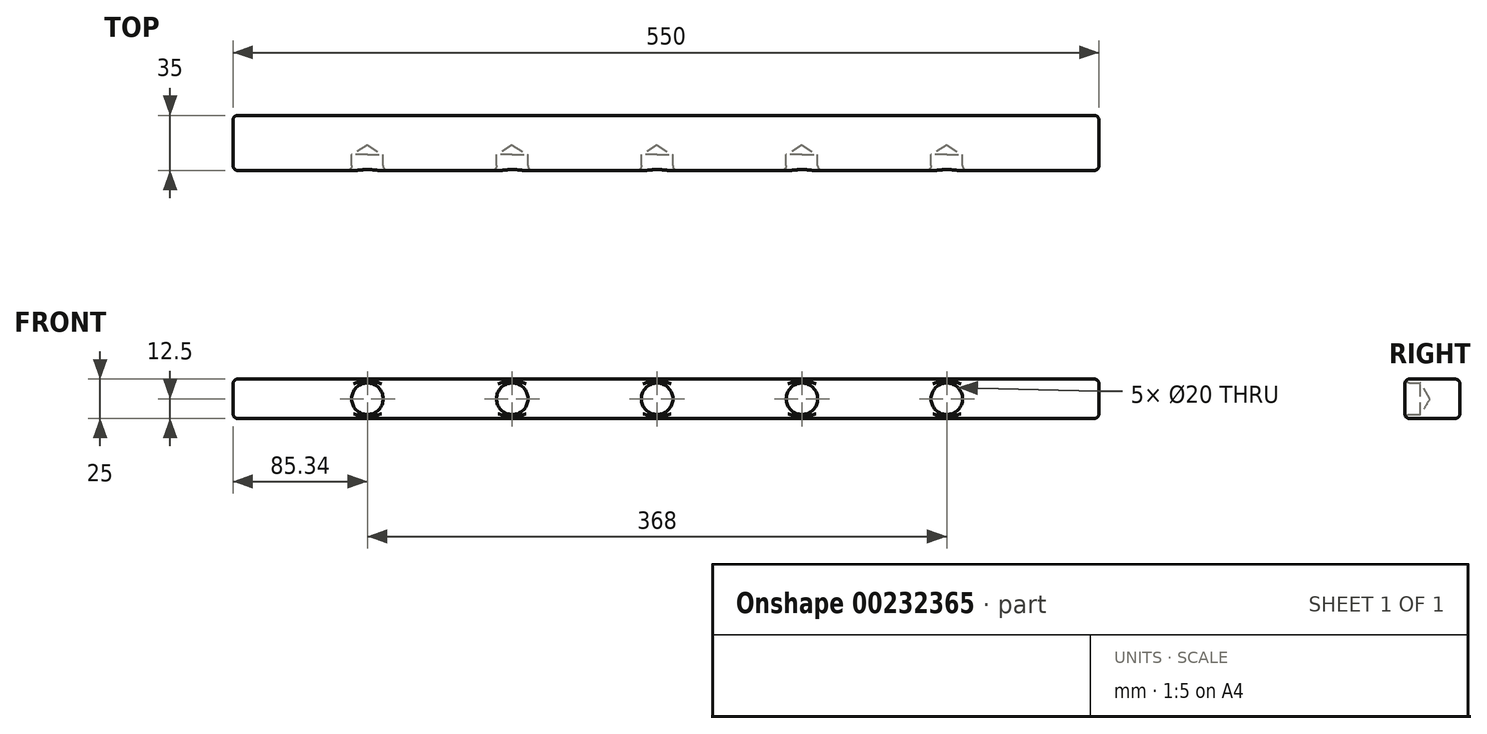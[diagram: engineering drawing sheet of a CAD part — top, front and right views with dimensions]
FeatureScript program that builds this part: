
annotation { "Feature Type Name" : "Feature", "Feature Type Description" : "" }
export const myFeature = defineFeature(function(context is Context, id is Id, definition is map)
    precondition{}
    {
        {
            var Q0;
            Q0=qCreatedBy(makeId("Front.planeOp"),FACE);
            var sketch = newSketch(context, id + "F0", { "sketchPlane" : qUnion([Q0])});
            skLineSegment(sketch, "E0.bottom", {"start": v(-269.34, 0) * mm, "end": v(280.66, 0) * mm});
            skLineSegment(sketch, "E0.top", {"start": v(-269.34, -25) * mm, "end": v(280.66, -25) * mm});
            skLineSegment(sketch, "E0.left", {"start": v(-269.34, 0) * mm, "end": v(-269.34, -25) * mm});
            skLineSegment(sketch, "E0.right", {"start": v(280.66, 0) * mm, "end": v(280.66, -25) * mm});
            skSolve(sketch);
        }
        {
            var Q0;
            Q0 = qSketchRegion(id + "F0", true);
            extrude(context, id + "F1", {"entities" : qUnion([Q0]), "oppositeDirection" : true, "depth" : 35 * mm});
        }
        {
            var Q0;
            Q0=qCreatedBy(makeId("Front.planeOp"),FACE);
            var sketch = newSketch(context, id + "F2", { "sketchPlane" : qUnion([Q0])});
            skPoint(sketch, "E1", {"position": v(0, -12.5) * mm});
            skPoint(sketch, "E2.1.0.0", {"position": v(92, -12.5) * mm});
            skPoint(sketch, "E2.2.0.0", {"position": v(184, -12.5) * mm});
            skLineSegment(sketch, "E2.direction1", {"start": v(0, -12.5) * mm, "end": v(92, -12.5) * mm, "construction": true});
            skPoint(sketch, "E3.1.0.0", {"position": v(-92, -12.5) * mm});
            skPoint(sketch, "E3.2.0.0", {"position": v(-184, -12.5) * mm});
            skLineSegment(sketch, "E3.direction1", {"start": v(0, -12.5) * mm, "end": v(-92, -12.5) * mm, "construction": true});
            skSolve(sketch);
        }
        {
            var Q0;
            Q0=sQuery(id+"F2.wireOp",VERTEX,"E1");
            var Q1;
            Q1=sQuery(id+"F2.wireOp",VERTEX,"E3.1.0.0");
            var Q2;
            Q2=sQuery(id+"F2.wireOp",VERTEX,"E3.2.0.0");
            var Q3;
            Q3=sQuery(id+"F2.wireOp",VERTEX,"E3.3.0.0");
            var Q4;
            Q4=sQuery(id+"F2.wireOp",VERTEX,"E2.1.0.0");
            var Q5;
            Q5=sQuery(id+"F2.wireOp",VERTEX,"E2.2.0.0");
            var Q6;
            Q6=sQuery(id+"F2.wireOp",VERTEX,"E2.3.0.0");
            var Q7;
            Q7=makeQuery(id+"F1.opExtrude","SWEPT_BODY",BODY,{"disambiguationData":[OSD([sQuery(id+"F0.wireOp",EDGE,"E0.bottom"),sQuery(id+"F0.wireOp",EDGE,"E0.top"),sQuery(id+"F0.wireOp",EDGE,"E0.left"),sQuery(id+"F0.wireOp",EDGE,"E0.right")])]});
            hole(context, id + "F3", {"style" : HoleStyle.SIMPLE, "endStyle" : HoleEndStyle.BLIND, "holeDiameter" : 20 * mm, "holeDepth" : 10 * mm, "locations" : qUnion([Q0, Q1, Q2, Q3, Q4, Q5, Q6]), "scope" : qUnion([Q7]), "startStyle" : HoleStartStyle.SKETCH});
        }
        {
            var Q0;
            Q0=makeQuery(id+"F1.opExtrude","CAP_FACE",FACE,{"disambiguationData":[OSD([sQuery(id+"F0.wireOp",EDGE,"E0.bottom"),sQuery(id+"F0.wireOp",EDGE,"E0.top"),sQuery(id+"F0.wireOp",EDGE,"E0.left"),sQuery(id+"F0.wireOp",EDGE,"E0.right")])],"isStart":false});
            var Q1;
            Q1=makeQuery(id+"F1.opExtrude","SWEPT_FACE",FACE,{"disambiguationData":[OSD([sQuery(id+"F0.wireOp",EDGE,"E0.right")])]});
            var Q2;
            Q2=makeQuery(id+"F1.opExtrude","SWEPT_FACE",FACE,{"disambiguationData":[OSD([sQuery(id+"F0.wireOp",EDGE,"E0.left")])]});
            var Q3;
            Q3=makeQuery(id+"F1.opExtrude","CAP_FACE",FACE,{"disambiguationData":[OSD([sQuery(id+"F0.wireOp",EDGE,"E0.bottom"),sQuery(id+"F0.wireOp",EDGE,"E0.top"),sQuery(id+"F0.wireOp",EDGE,"E0.left"),sQuery(id+"F0.wireOp",EDGE,"E0.right")])],"isStart":true});
            fillet(context, id + "F4", {"entities" : qUnion([Q0, Q1, Q2, Q3]), "radius" : 3 * mm, "tangentPropagation" : true, "allowEdgeOverflow" : false});
        }
    });
